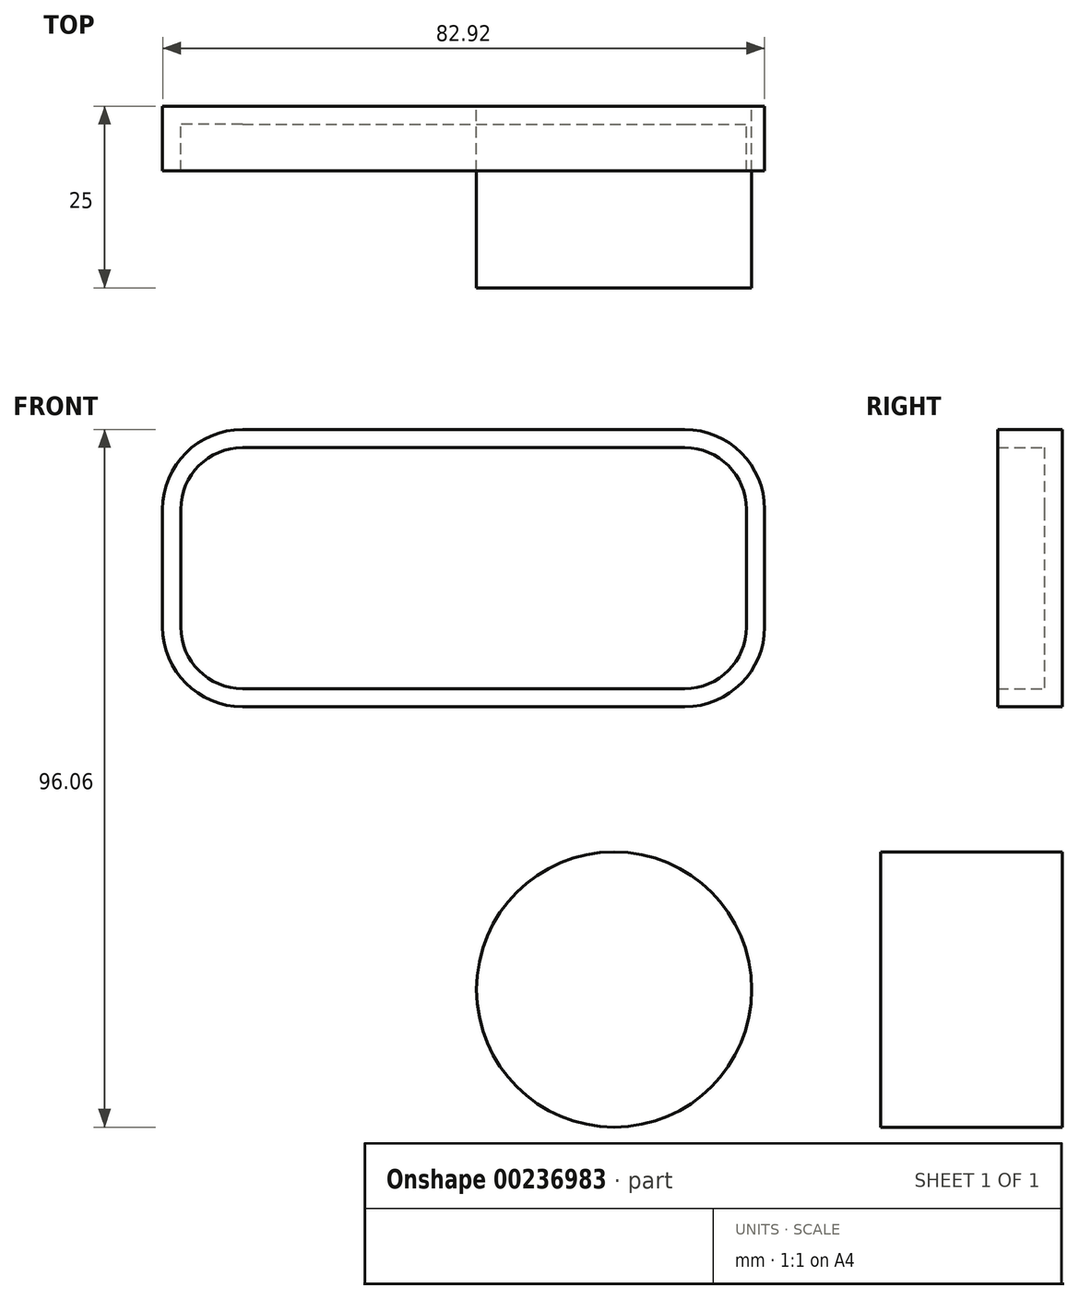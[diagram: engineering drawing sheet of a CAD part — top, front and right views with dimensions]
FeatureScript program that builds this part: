
annotation { "Feature Type Name" : "Feature", "Feature Type Description" : "" }
export const myFeature = defineFeature(function(context is Context, id is Id, definition is map)
    precondition{}
    {
        {
            var Q0;
            Q0=qCreatedBy(makeId("Front.planeOp"),FACE);
            var sketch = newSketch(context, id + "F0", { "sketchPlane" : qUnion([Q0])});
            skLineSegment(sketch, "E0.bottom", {"start": v(-51.2, 45.13) * mm, "end": v(-21.24, 45.13) * mm});
            skLineSegment(sketch, "E0.top", {"start": v(-51.2, 6.95) * mm, "end": v(-21.24, 6.95) * mm});
            skLineSegment(sketch, "E0.left", {"start": v(-62.2, 34.13) * mm, "end": v(-62.2, 17.95) * mm});
            skLineSegment(sketch, "E1.bottom", {"start": v(-21.24, 45.13) * mm, "end": v(9.73, 45.13) * mm});
            skLineSegment(sketch, "E1.top", {"start": v(-21.24, 6.95) * mm, "end": v(9.73, 6.95) * mm});
            skLineSegment(sketch, "E1.right", {"start": v(20.73, 34.13) * mm, "end": v(20.73, 17.95) * mm});
            skPoint(sketch, "E2.oppositeSnap0", {"position": v(-41.71, 45.13) * mm});
            skLineSegment(sketch, "E2.bottom", {"start": v(-41.71, 45.13) * mm, "end": v(-41.71, 45.13) * mm});
            skLineSegment(sketch, "E3.top", {"start": v(-4.04, 45.13) * mm, "end": v(-4.04, 45.13) * mm});
            skLineSegment(sketch, "E4.right", {"start": v(11.12, 45.13) * mm, "end": v(11.12, 45.13) * mm});
            skArc(sketch, "E5.filletArc", {"start": v(-51.2, 45.13) * mm, "mid": v(-58.97, 41.9) * mm, "end": v(-62.2, 34.13) * mm});
            skArc(sketch, "E6.filletArc", {"start": v(-62.2, 17.95) * mm, "mid": v(-58.97, 10.17) * mm, "end": v(-51.2, 6.95) * mm});
            skArc(sketch, "E7.filletArc", {"start": v(20.73, 34.13) * mm, "mid": v(17.5, 41.9) * mm, "end": v(9.73, 45.13) * mm});
            skArc(sketch, "E8.filletArc", {"start": v(9.73, 6.95) * mm, "mid": v(17.5, 10.17) * mm, "end": v(20.73, 17.95) * mm});
            skSolve(sketch);
        }
        {
            var Q0;
            Q0=makeQuery(id+"F0.imprint","IMPRINT",FACE,{"disambiguationData":[TD([[makeQuery(id+"F0.imprint","IMPRINT",EDGE,{"derivedFrom":sQuery(id+"F0.wireOp",EDGE,"E0.bottom")}),-1.0]])]});
            extrude(context, id + "F1", {"entities" : qUnion([Q0]), "depth" : 8.9 * mm});
        }
        {
            var Q0;
            Q0=makeQuery(id+"F1.opExtrude","CAP_FACE",FACE,{"disambiguationData":[OSD([sQuery(id+"F0.wireOp",EDGE,"E0.bottom"),sQuery(id+"F0.wireOp",EDGE,"E0.top"),sQuery(id+"F0.wireOp",EDGE,"E0.left"),sQuery(id+"F0.wireOp",EDGE,"E1.bottom"),sQuery(id+"F0.wireOp",EDGE,"E1.top"),sQuery(id+"F0.wireOp",EDGE,"E1.right"),sQuery(id+"F0.wireOp",EDGE,"E5.filletArc"),sQuery(id+"F0.wireOp",EDGE,"E6.filletArc"),sQuery(id+"F0.wireOp",EDGE,"E7.filletArc"),sQuery(id+"F0.wireOp",EDGE,"E8.filletArc")])],"isStart":false});
            shell(context, id + "F2", {"entities" : qUnion([Q0]), "thickness" : 2.5 * mm});
        }
        {
            var Q0;
            Q0=qCreatedBy(makeId("Front.planeOp"),FACE);
            var sketch = newSketch(context, id + "F3", { "sketchPlane" : qUnion([Q0])});
            skCircle(sketch, "E9", {"center": v(0, -31.98) * mm, "radius": 18.95 * mm});
            skSolve(sketch);
        }
        {
            var Q0;
            Q0=makeQuery(id+"F3.imprint","IMPRINT",FACE,{"disambiguationData":[TD([[makeQuery(id+"F3.imprint","IMPRINT",EDGE,{"derivedFrom":sQuery(id+"F3.wireOp",EDGE,"E9")}),1.0]])]});
            extrude(context, id + "F4", {"entities" : qUnion([Q0]), "depth" : 25 * mm});
        }
    });
